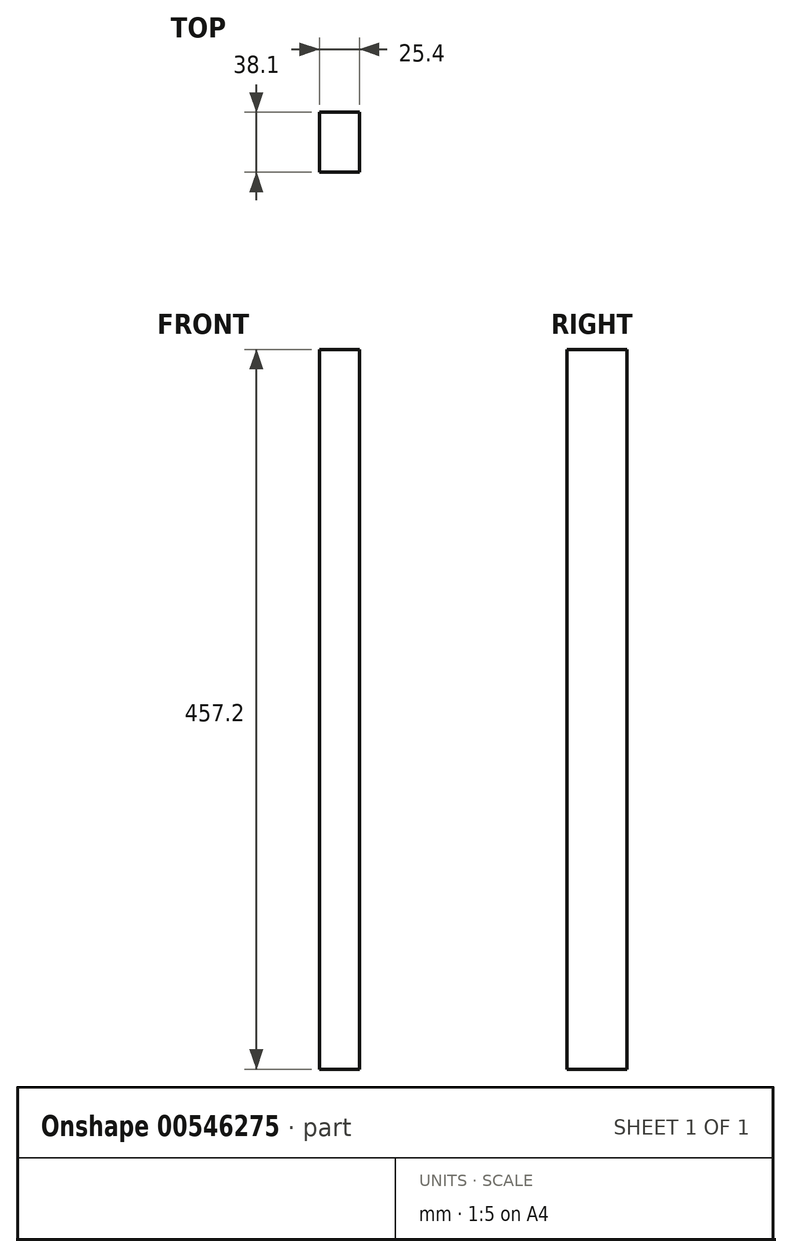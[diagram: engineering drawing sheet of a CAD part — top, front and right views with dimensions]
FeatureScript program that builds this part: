
annotation { "Feature Type Name" : "Feature", "Feature Type Description" : "" }
export const myFeature = defineFeature(function(context is Context, id is Id, definition is map)
    precondition{}
    {
        {
            var Q0;
            Q0=qCreatedBy(makeId("Top.planeOp"),FACE);
            var sketch = newSketch(context, id + "F0", { "sketchPlane" : qUnion([Q0])});
            skLineSegment(sketch, "E0", {"start": v(-38.28, 16.72) * mm, "end": v(-38.28, 54.82) * mm});
            skLineSegment(sketch, "E1", {"start": v(-38.28, 54.82) * mm, "end": v(-12.88, 54.82) * mm});
            skLineSegment(sketch, "E2", {"start": v(-12.88, 54.82) * mm, "end": v(-12.88, 16.72) * mm});
            skLineSegment(sketch, "E3", {"start": v(-12.88, 16.72) * mm, "end": v(-38.28, 16.72) * mm});
            skSolve(sketch);
        }
        {
            var Q0;
            Q0=makeQuery(id+"F0.imprint","IMPRINT",FACE,{"disambiguationData":[TD([[makeQuery(id+"F0.imprint","IMPRINT",EDGE,{"derivedFrom":sQuery(id+"F0.wireOp",EDGE,"E0")}),-1.0]])]});
            extrude(context, id + "F1", {"entities" : qUnion([Q0]), "depth" : 457.2 * mm, "offsetDistance" : 25.4 * mm});
        }
    });
